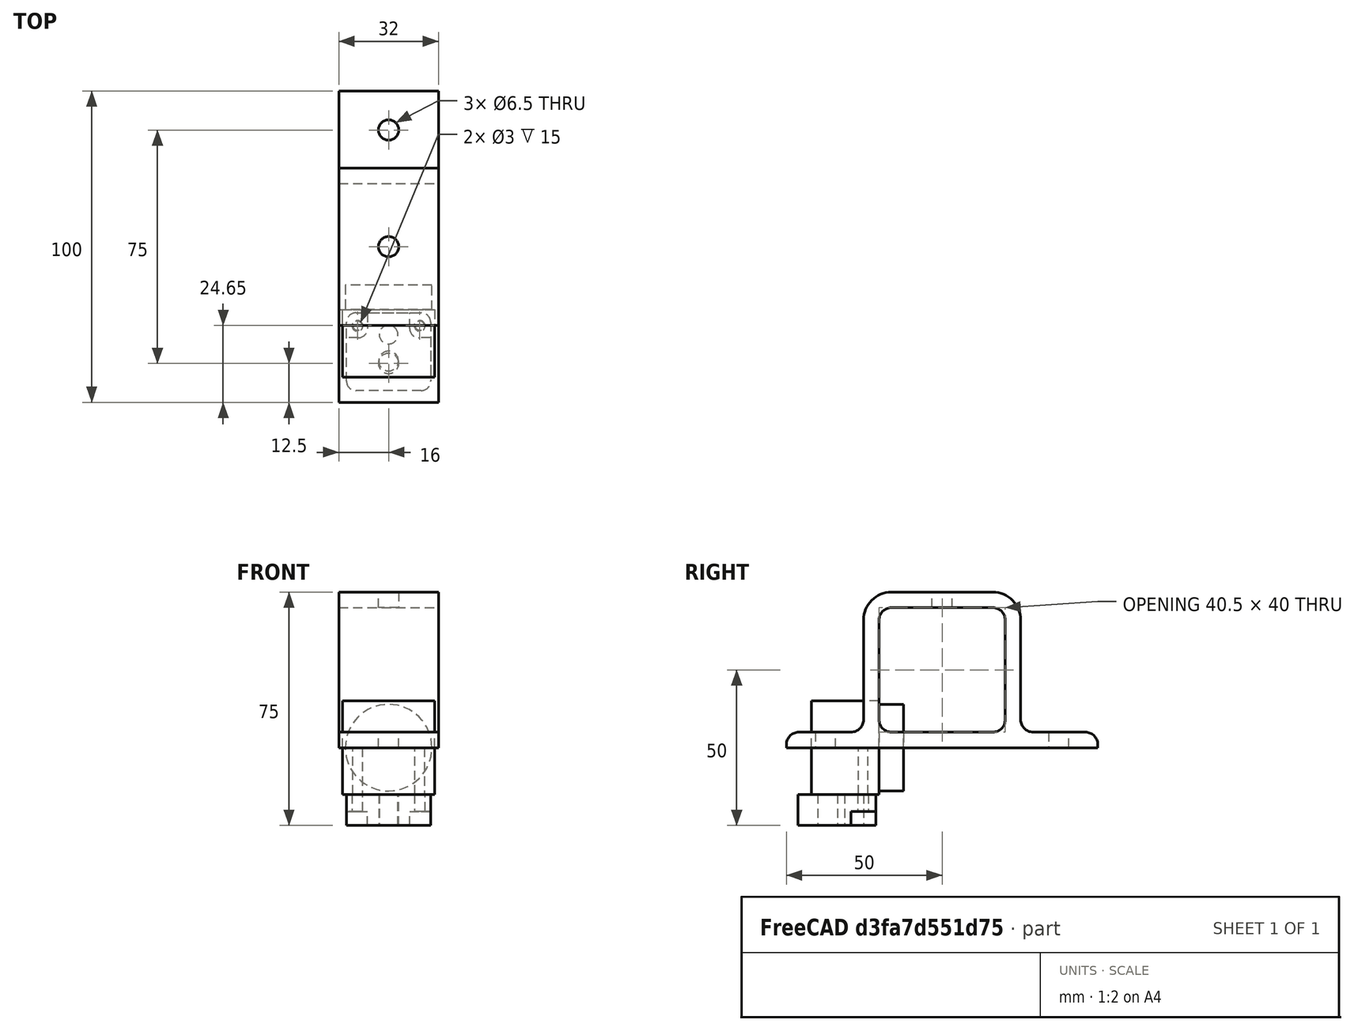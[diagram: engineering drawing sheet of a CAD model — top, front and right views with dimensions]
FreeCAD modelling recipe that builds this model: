
FCSTD DOCUMENT  (FreeCAD 0.19R)
Label: cam_single_mt_optical_table
License: All rights reserved
LicenseURL: http://en.wikipedia.org/wiki/All_rights_reserved
objects: Sketcher::SketchObject×10, PartDesign::Pocket×6, PartDesign::Pad×4, PartDesign::Body×3, App::Part×2, Spreadsheet::Sheet×1, PartDesign::Plane×1, Mesh::Feature×1
note: 34 computed .brp shape members not serialized (recipe doc carries the construction recipe); baked Part::Feature solids carry a one-line shape summary decoded from their .brp

FEATURE [Spreadsheet::Sheet] Spreadsheet  label="pp"
  cells = A2=std rad; B2(std_rad)==3mm; A4=Tol rail width; B4(tol_rail_width)==0.5mm; A5=rail width; B5(rail_width)==40mm; A6=tot width; B6(tot_width)==rail_width + tol_rail_width; A8=std wall thick; B8(wall_thick)==5mm; A10=mt hole loc tol; B10(tol_mt_hole_loc)==0.25mm; A11=mt hole diam; B11(mt_hole_diam)==9mm; C11=for M8; A13=a key height clear; B13(key_height_clear)==40mm; D13=# This is the parameter to change; A15=cam mt hole; B15(cam_mt_hole)==6.5mm; C15=for M6; A17=mt width; B17(mt_width)==32mm
FEATURE [Sketcher::SketchObject] Sketch
  FullyConstrained = true
  MapMode = 5
  Placement = pos=(0,0,0) rot=(0.57735,0.57735,0.57735;2.0944rad)
  expr: Constraints[62] = 50 - 20.25
  sketch-geometry (26):
    g0: LineSegment StartX=-5 StartY=9 StartZ=0 EndX=-5 EndY=41 EndZ=0
    g1: LineSegment StartX=45.5 StartY=9 StartZ=0 EndX=45.5 EndY=41 EndZ=0
    g2: LineSegment StartX=4 StartY=50 StartZ=0 EndX=36.5 EndY=50 EndZ=0
    g3: ArcOfCircle CenterX=4 CenterY=41 CenterZ=0 NormalX=0 NormalY=0 NormalZ=1 AngleXU=0 Radius=4 StartAngle=1.5708 EndAngle=3.14159
    g4: LineSegment StartX=4 StartY=45 StartZ=0 EndX=36.5 EndY=45 EndZ=0
    g5: ArcOfCircle CenterX=36.5 CenterY=41 CenterZ=0 NormalX=0 NormalY=0 NormalZ=1 AngleXU=0 Radius=4 StartAngle=4e-16 EndAngle=1.5708
    g6: LineSegment StartX=40.5 StartY=41 StartZ=0 EndX=40.5 EndY=9 EndZ=0
    g7: ArcOfCircle CenterX=36.5 CenterY=9 CenterZ=0 NormalX=0 NormalY=0 NormalZ=1 AngleXU=0 Radius=4 StartAngle=4.71239 EndAngle=6.28319
    g8: LineSegment StartX=36.5 StartY=5 StartZ=0 EndX=4 EndY=5 EndZ=0
    g9: ArcOfCircle CenterX=4 CenterY=9 CenterZ=0 NormalX=0 NormalY=0 NormalZ=1 AngleXU=0 Radius=4 StartAngle=3.14159 EndAngle=4.71239
    g10: LineSegment StartX=0 StartY=9 StartZ=0 EndX=0 EndY=41 EndZ=0
    g11: GeomPoint X=0 Y=45 Z=0
    g12: GeomPoint X=40.5 Y=5 Z=0
    g13: ArcOfCircle CenterX=36.5 CenterY=41 CenterZ=0 NormalX=0 NormalY=0 NormalZ=1 AngleXU=0 Radius=9 StartAngle=0 EndAngle=1.5708
    g14: ArcOfCircle CenterX=4 CenterY=41 CenterZ=0 NormalX=0 NormalY=0 NormalZ=1 AngleXU=0 Radius=9 StartAngle=1.5708 EndAngle=3.14159
    g15: LineSegment StartX=4 StartY=45 StartZ=0 EndX=4 EndY=50 EndZ=0
    g16: LineSegment StartX=0 StartY=41 StartZ=0 EndX=-5 EndY=41 EndZ=0
    g17: LineSegment StartX=-29.75 StartY=0 StartZ=0 EndX=70.25 EndY=0 EndZ=0
    g18: LineSegment StartX=70.25 StartY=0 StartZ=0 EndX=70.25 EndY=1 EndZ=0
    g19: LineSegment StartX=-29.75 StartY=0 StartZ=0 EndX=-29.75 EndY=1 EndZ=0
    g20: LineSegment StartX=-25.75 StartY=5 StartZ=0 EndX=-9 EndY=5 EndZ=0
    g21: LineSegment StartX=49.5 StartY=5 StartZ=0 EndX=66.25 EndY=5 EndZ=0
    g22: ArcOfCircle CenterX=49.5 CenterY=9 CenterZ=0 NormalX=0 NormalY=0 NormalZ=1 AngleXU=0 Radius=4 StartAngle=3.14159 EndAngle=4.71239
    g23: ArcOfCircle CenterX=-9 CenterY=9 CenterZ=0 NormalX=0 NormalY=0 NormalZ=1 AngleXU=0 Radius=4 StartAngle=4.71239 EndAngle=6.28319
    g24: ArcOfCircle CenterX=66.25 CenterY=1 CenterZ=0 NormalX=0 NormalY=0 NormalZ=1 AngleXU=0 Radius=4 StartAngle=0 EndAngle=1.5708
    g25: ArcOfCircle CenterX=-25.75 CenterY=1 CenterZ=0 NormalX=0 NormalY=0 NormalZ=1 AngleXU=0 Radius=4 StartAngle=1.5708 EndAngle=3.14159
  constraints (64):
    c: Vertical(g0)
    c: Vertical(g1)
    c: Horizontal(g2)
    c: Tangent(g3,g4) = 1.5708
    c: Tangent(g4,g5) = 1.5708
    c: Tangent(g5,g6) = 1.5708
    c: Tangent(g6,g7) = 1.5708
    c: Tangent(g7,g8) = 1.5708
    c: Tangent(g8,g9) = 1.5708
    c: Tangent(g9,g10) = 1.5708
    c: Tangent(g10,g3) = 1.5708
    c: Horizontal(g4)
    c: Horizontal(g8)
    c: Vertical(g6)
    c: Vertical(g10)
    c: Equal(g3,g5)
    c: Equal(g5,g7)
    c: Equal(g7,g9)
    c: PointOnObject(g11,g4)
    c: PointOnObject(g11,g10)
    c: PointOnObject(g12,g6)
    c: PointOnObject(g12,g8)
    c: PointOnObject(g11,g-2)
    c: Tangent(g0,g14) = 1.5708
    c: Tangent(g2,g14) = 1.5708
    c: Coincident(g15,g3)
    c: Coincident(g15,g2)
    c: Coincident(g16,g3)
    c: Coincident(g16,g0)
    c: Vertical(g15)
    c: Horizontal(g16)
    c: Tangent(g13,g1) = -1.5708
    c: Tangent(g13,g2) = 1.5708
    c: Equal(g14,g13)
    c: DistanceY(g7,g4) = 40
    c: DistanceX(g3,g5) = 40.5
    c: PointOnObject(g17,g-1)
    c: PointOnObject(g17,g-1)
    c: Coincident(g18,g17)
    c: Vertical(g18)
    c: Coincident(g19,g17)
    c: Vertical(g19)
    c: Horizontal(g21)
    c: Horizontal(g20)
    c: Tangent(g21,g22) = -1.5708
    c: Tangent(g1,g22) = 1.5708
    c: Tangent(g20,g23) = -1.5708
    c: Tangent(g0,g23) = -1.5708
    c: Tangent(g18,g24) = -1.5708
    c: Tangent(g21,g24) = 1.5708
    c: Tangent(g19,g25) = 1.5708
    c: Tangent(g20,g25) = 1.5708
    c: Equal(g9,g23)
    c: Horizontal(g6,g1)
    c: Equal(g7,g22)
    c: Horizontal(g9,g0)
    c: Horizontal(g19,g18)
    c: Equal(g25,g23)
    c: DistanceY(g17,g20) = 5
    c: DistanceX(g5,g1) = 5
    c: DistanceX(g16,g16) = 5
    c: DistanceX(g17,g17) = 100
    c: DistanceX(g17,g9) = 29.75
    c: Radius(g3) = 4
FEATURE [Sketcher::SketchObject] Sketch001
  FullyConstrained = true
  MapMode = 5
  sketch-geometry (4):
    g0: LineSegment StartX=-14.8 StartY=0 StartZ=0 EndX=14.8 EndY=0 EndZ=0
    g1: LineSegment StartX=14.8 StartY=0 StartZ=0 EndX=14.8 EndY=-21.7 EndZ=0
    g2: LineSegment StartX=14.8 StartY=-21.7 StartZ=0 EndX=-14.8 EndY=-21.7 EndZ=0
    g3: LineSegment StartX=-14.8 StartY=-21.7 StartZ=0 EndX=-14.8 EndY=0 EndZ=0
  constraints (11):
    c: Coincident(g0,g1)
    c: Coincident(g1,g2)
    c: Coincident(g2,g3)
    c: Coincident(g3,g0)
    c: Horizontal(g0)
    c: Horizontal(g2)
    c: Vertical(g1)
    c: Vertical(g3)
    c: Distance(g0) = 29.6
    c: Distance(g1) = 21.7
    c: Symmetric(g0,g0,g-1)
FEATURE [PartDesign::Pad] Pad001
  Direction = (0,0,1)
  Length = 30
  Length2 = 100
  Midplane = true
  Profile = -> Sketch001
  Type = 0
FEATURE [Sketcher::SketchObject] Sketch003
  FullyConstrained = true
  MapMode = 5
  Placement = pos=(0,0,0) rot=(1,0,0;1.5708rad)
  sketch-geometry (1):
    g0: Circle CenterX=0 CenterY=0 CenterZ=0 NormalX=0 NormalY=0 NormalZ=1 AngleXU=0 Radius=13.9
  constraints (2):
    c: Coincident(g0,g-1)
    c: Diameter(g0) = 27.8
FEATURE [PartDesign::Pad] Pad002
  BaseFeature = -> Pad001
  Direction = (0,-1,2e-16)
  Length = 7.9
  Length2 = 100
  Profile = -> Sketch003
  Reversed = true
  Type = 0
FEATURE [Sketcher::SketchObject] Sketch004
  FullyConstrained = true
  MapMode = 5
  sketch-geometry (4):
    g0: Circle CenterX=-10 CenterY=-5.1 CenterZ=0 NormalX=0 NormalY=0 NormalZ=1 AngleXU=0 Radius=1.5
    g1: Circle CenterX=10 CenterY=-5.1 CenterZ=0 NormalX=0 NormalY=0 NormalZ=1 AngleXU=0 Radius=1.5
    g2: LineSegment StartX=-10 StartY=-5.1 StartZ=0 EndX=10 EndY=-5.1 EndZ=0
    g3: LineSegment StartX=0 StartY=0 StartZ=0 EndX=0 EndY=-5.1 EndZ=0
  constraints (10):
    c: Equal(g0,g1)
    c: Coincident(g2,g0)
    c: Coincident(g2,g1)
    c: Horizontal(g2)
    c: Coincident(g3,g-1)
    c: PointOnObject(g3,g-2)
    c: Symmetric(g0,g1,g3)
    c: Diameter(g1) = 3
    c: DistanceX(g0,g1) = 20
    c: DistanceY(g3,g-1) = 5.1
FEATURE [PartDesign::Pocket] Pocket
  BaseFeature = -> Pad002
  Length = 5
  Length2 = 100
  Profile = -> Sketch004
  Type = 1
FEATURE [PartDesign::Body] Body001
  Group = -> [Sketch001,Pad001,Sketch003,Pad002,Sketch004,Pocket]
  Origin = -> Origin003
  Tip = -> Pocket
FEATURE [Sketcher::SketchObject] Sketch010
  FullyConstrained = true
  MapMode = 5
  sketch-geometry (2):
    g0: Circle CenterX=0 CenterY=-7 CenterZ=0 NormalX=0 NormalY=0 NormalZ=1 AngleXU=0 Radius=3
    g1: Circle CenterX=0 CenterY=-15.5 CenterZ=0 NormalX=0 NormalY=0 NormalZ=1 AngleXU=0 Radius=3.175
  constraints (6):
    c: PointOnObject(g0,g-2)
    c: PointOnObject(g1,g-2)
    c: Diameter(g0) = 6
    c: Diameter(g1) = 6.35
    c: DistanceY(g0,g-1) = 7
    c: DistanceY(g1,g0) = 8.5
FEATURE [Sketcher::SketchObject] Sketch011
  FullyConstrained = true
  MapMode = 5
  sketch-geometry (4):
    g0: Circle CenterX=-10 CenterY=-4.2 CenterZ=0 NormalX=0 NormalY=0 NormalZ=1 AngleXU=0 Radius=1.7
    g1: Circle CenterX=10 CenterY=-4.2 CenterZ=0 NormalX=0 NormalY=0 NormalZ=1 AngleXU=0 Radius=1.7
    g2: LineSegment StartX=-10 StartY=-4.2 StartZ=0 EndX=10 EndY=-4.2 EndZ=0
    g3: LineSegment StartX=0 StartY=0 StartZ=0 EndX=0 EndY=-4.2 EndZ=0
  constraints (10):
    c: Coincident(g2,g0)
    c: Coincident(g2,g1)
    c: Coincident(g3,g-1)
    c: PointOnObject(g3,g-2)
    c: Horizontal(g2)
    c: Equal(g1,g0)
    c: Symmetric(g0,g1,g3)
    c: Diameter(g1) = 3.4
    c: DistanceX(g0,g1) = 20
    c: DistanceY(g3,g-1) = 4.2
FEATURE [Sketcher::SketchObject] Sketch012
  FullyConstrained = true
  MapMode = 5
  sketch-geometry (8):
    g0: LineSegment StartX=-10.5 StartY=-9e-16 StartZ=0 EndX=10.5 EndY=-9e-16 EndZ=0
    g1: LineSegment StartX=13.5 StartY=-3 StartZ=0 EndX=13.5 EndY=-22 EndZ=0
    g2: LineSegment StartX=10.5 StartY=-25 StartZ=0 EndX=-10.5 EndY=-25 EndZ=0
    g3: LineSegment StartX=-13.5 StartY=-22 StartZ=0 EndX=-13.5 EndY=-3 EndZ=0
    g4: ArcOfCircle CenterX=-10.5 CenterY=-3 CenterZ=0 NormalX=0 NormalY=0 NormalZ=1 AngleXU=0 Radius=3 StartAngle=1.5708 EndAngle=3.14159
    g5: ArcOfCircle CenterX=10.5 CenterY=-3 CenterZ=0 NormalX=0 NormalY=0 NormalZ=1 AngleXU=0 Radius=3 StartAngle=0 EndAngle=1.5708
    g6: ArcOfCircle CenterX=10.5 CenterY=-22 CenterZ=0 NormalX=0 NormalY=0 NormalZ=1 AngleXU=0 Radius=3 StartAngle=4.71239 EndAngle=6.28319
    g7: ArcOfCircle CenterX=-10.5 CenterY=-22 CenterZ=0 NormalX=0 NormalY=0 NormalZ=1 AngleXU=0 Radius=3 StartAngle=3.14159 EndAngle=4.71239
  constraints (19):
    c: Horizontal(g0)
    c: Horizontal(g2)
    c: Vertical(g1)
    c: Vertical(g3)
    c: Tangent(g3,g4) = 1.5708
    c: Tangent(g0,g4) = 1.5708
    c: Tangent(g0,g5) = 1.5708
    c: Tangent(g1,g5) = 1.5708
    c: Tangent(g1,g6) = 1.5708
    c: Tangent(g2,g6) = 1.5708
    c: Tangent(g2,g7) = 1.5708
    c: Tangent(g3,g7) = 1.5708
    c: Equal(g4,g5)
    c: Equal(g5,g6)
    c: Equal(g6,g7)
    c: Symmetric(g0,g0,g-1)
    c: Radius(g5) = 3
    c: DistanceX(g3,g1) = 27
    c: DistanceY(g2,g0) = 25
FEATURE [PartDesign::Pad] Pad005
  Direction = (0,0,1)
  Length = 10
  Length2 = 100
  Profile = -> Sketch012
  Type = 0
FEATURE [PartDesign::Pocket] Pocket005
  BaseFeature = -> Pad005
  Length = 5
  Length2 = 100
  Profile = -> Sketch010
  Reversed = true
  Type = 1
FEATURE [PartDesign::Pocket] Pocket006
  BaseFeature = -> Pocket005
  Length = 5
  Length2 = 100
  Profile = -> Sketch011
  Reversed = true
  Type = 1
FEATURE [Sketcher::SketchObject] Sketch013
  FullyConstrained = true
  MapMode = 5
  sketch-geometry (12):
    g0: LineSegment StartX=-6.75 StartY=5 StartZ=0 EndX=-6.75 EndY=-5 EndZ=0
    g1: LineSegment StartX=-9.75 StartY=-8 StartZ=0 EndX=-20 EndY=-8 EndZ=0
    g2: LineSegment StartX=-20 StartY=-8 StartZ=0 EndX=-20 EndY=10 EndZ=0
    g3: LineSegment StartX=-20 StartY=10 StartZ=0 EndX=20 EndY=10 EndZ=0
    g4: LineSegment StartX=20 StartY=10 StartZ=0 EndX=20 EndY=-8 EndZ=0
    g5: LineSegment StartX=20 StartY=-8 StartZ=0 EndX=9.75 EndY=-8 EndZ=0
    g6: LineSegment StartX=6.75 StartY=-5 StartZ=0 EndX=6.75 EndY=5 EndZ=0
    g7: LineSegment StartX=6.75 StartY=5 StartZ=0 EndX=-6.75 EndY=5 EndZ=0
    g8: ArcOfCircle CenterX=-9.75 CenterY=-5 CenterZ=0 NormalX=0 NormalY=0 NormalZ=1 AngleXU=0 Radius=3 StartAngle=4.71239 EndAngle=6.28319
    g9: ArcOfCircle CenterX=9.75 CenterY=-5 CenterZ=0 NormalX=0 NormalY=0 NormalZ=1 AngleXU=0 Radius=3 StartAngle=3.14159 EndAngle=4.71239
    g10: LineSegment StartX=-6.75 StartY=-5 StartZ=0 EndX=6.75 EndY=-5 EndZ=0
    g11: LineSegment StartX=0 StartY=0 StartZ=0 EndX=0 EndY=-5 EndZ=0
  constraints (32):
    c: Vertical(g0)
    c: Horizontal(g1)
    c: Coincident(g2,g1)
    c: Vertical(g2)
    c: Coincident(g3,g2)
    c: Horizontal(g3)
    c: Coincident(g4,g3)
    c: Vertical(g4)
    c: Coincident(g5,g4)
    c: Horizontal(g5)
    c: Vertical(g6)
    c: Coincident(g7,g6)
    c: Coincident(g7,g0)
    c: Horizontal(g7)
    c: Tangent(g1,g8) = 1.5708
    c: Tangent(g0,g8) = 1.5708
    c: Tangent(g6,g9) = 1.5708
    c: Tangent(g5,g9) = 1.5708
    c: Equal(g9,g8)
    c: Coincident(g10,g0)
    c: Coincident(g10,g6)
    c: Horizontal(g10)
    c: Coincident(g11,g-1)
    c: PointOnObject(g11,g-2)
    c: Symmetric(g0,g6,g11)
    c: Radius(g9) = 3
    c: DistanceX(g0,g6) = 13.5
    c: Equal(g1,g5)
    c: DistanceY(g-1,g6) = 5
    c: DistanceY(g-1,g3) = 10
    c: DistanceX(g2,g3) = 40
    c: DistanceY(g4,g-1) = 8
FEATURE [PartDesign::Pocket] Pocket004
  BaseFeature = -> Pocket006
  Length = 4.5
  Length2 = 100
  Profile = -> Sketch013
  Reversed = true
  Type = 0
FEATURE [PartDesign::Body] Body004
  Group = -> [Sketch012,Pad005,Sketch010,Pocket005,Sketch011,Pocket006,Sketch013,Pocket004]
  Origin = -> Origin007
  Placement = pos=(0,-1,-25) rot=(0,0,1;0rad)
  Tip = -> Pocket004
FEATURE [App::Part] Part001  label="camera-cube"
  Group = -> [Body001,Body004]
  Origin = -> Origin002
  Placement = pos=(-2.7e-15,12.2,75) rot=(0,0,1;3.14159rad)
FEATURE [PartDesign::Pad] Pad  label="Pad_MainBody"
  Direction = (1,0,0)
  Length = 32
  Length2 = 10
  Midplane = true
  Placement = pos=(0,0,0) rot=(0.57735,0.57735,0.57735;2.0944rad)
  Profile = -> Sketch
  Type = 0
  expr: Length = <<pp>>.mt_width
FEATURE [PartDesign::Plane] DatumPlane  label="TopSurf"
  AttachmentOffset = pos=(0,0,50) rot=(0,0,1;0rad)
  Length = 64.1421
  MapMode = 5
  Placement = pos=(0,0,50) rot=(0,0,1;0rad)
  ResizeMode = 0
  Width = 114.142
  expr: .AttachmentOffset.Base.z = <<pp>>.key_height_clear + 2 * <<pp>>.wall_thick
FEATURE [Sketcher::SketchObject] Sketch014
  FullyConstrained = true
  MapMode = 5
  Placement = pos=(0,0,50) rot=(0,0,1;0rad)
  expr: Constraints[1] = <<pp>>.cam_mt_hole
  expr: Constraints[2] = <<pp>>.tot_width / 2
  sketch-geometry (1):
    g0: Circle CenterX=0 CenterY=20.25 CenterZ=0 NormalX=0 NormalY=0 NormalZ=1 AngleXU=0 Radius=3.25
  constraints (3):
    c: PointOnObject(g0,g-2)
    c: Diameter(g0) = 6.5
    c: DistanceY(g-1,g0) = 20.25
FEATURE [PartDesign::Pocket] Pocket007  label="Pocket_CamMt_M6"
  BaseFeature = -> Pad
  Length = 10
  Length2 = 5
  Placement = pos=(0,0,0) rot=(0.57735,0.57735,0.57735;2.0944rad)
  Profile = -> Sketch014
  Type = 0
  expr: Length = 2 * <<pp>>.wall_thick
FEATURE [Mesh::Feature] Mesh  label="cam_mt (Meshed)"
FEATURE [Sketcher::SketchObject] Sketch017
  FullyConstrained = true
  MapMode = 5
  Placement = pos=(-6e-16,6e-16,5) rot=(0,0,-1;1.5708rad)
  Support = -> [Pocket007]
  expr: Constraints[5] = 75 / 2 - 40.5 / 2
  sketch-geometry (2):
    g0: Circle CenterX=-57.75 CenterY=0 CenterZ=0 NormalX=0 NormalY=0 NormalZ=1 AngleXU=0 Radius=3.25
    g1: Circle CenterX=17.25 CenterY=0 CenterZ=0 NormalX=0 NormalY=0 NormalZ=1 AngleXU=0 Radius=3.25
  constraints (6):
    c: PointOnObject(g0,g-1)
    c: PointOnObject(g1,g-1)
    c: Diameter(g1) = 6.5
    c: Diameter(g0) = 6.5
    c: DistanceX(g0,g1) = 75
    c: DistanceX(g-1,g1) = 17.25
FEATURE [PartDesign::Pocket] Pocket008
  BaseFeature = -> Pocket007
  Length = 5
  Length2 = 100
  Placement = pos=(0,0,0) rot=(0.57735,0.57735,0.57735;2.0944rad)
  Profile = -> Sketch017
  Type = 0
FEATURE [PartDesign::Body] Body  label="cam_mt"
  Group = -> [Sketch,Pad,DatumPlane,Sketch014,Pocket007,Sketch017,Pocket008]
  Origin = -> Origin001
  Tip = -> Pocket008
FEATURE [App::Part] Part  label="cam_mt_part"
  Group = -> [Body]
  Origin = -> Origin
